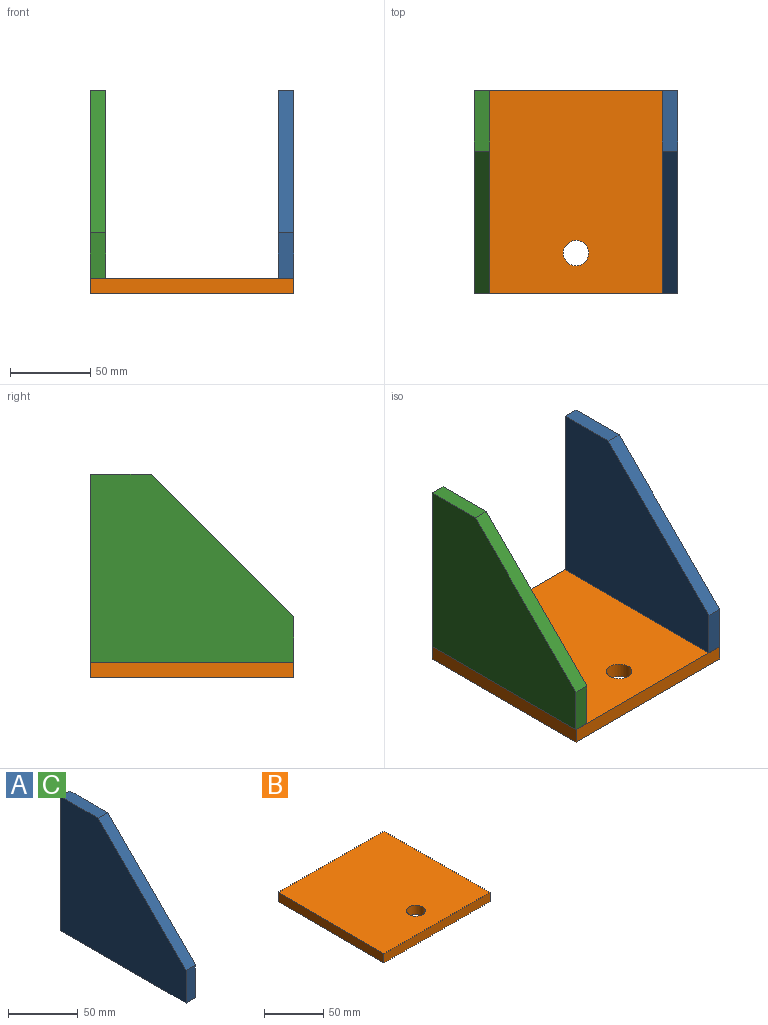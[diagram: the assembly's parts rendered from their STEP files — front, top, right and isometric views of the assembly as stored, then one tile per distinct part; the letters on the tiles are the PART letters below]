
ASSEMBLY  parts=3 mates=1
PART A: 7 faces, bbox 9.5x127x117.5 mm
  f0: plane 88.9x88.9mm, normal (0,-0.71,0.71), area 1197.5mm2, adj f1,f2,f4,f5
  f1: plane 38.1x9.53mm, normal (0,0,1), area 362.9mm2, adj f0,f2,f3,f4
  f2: plane 127x117.48mm, normal (-1,0,0), area 10967.7mm2, adj f0,f1,f3,f5,f6
  f3: plane 117.48x9.53mm, normal (0,1,0), area 1118.9mm2, adj f1,f2,f4,f6
  f4: plane 127x117.48mm, normal (1,0,0), area 10967.7mm2, adj f0,f1,f3,f5,f6
  f5: plane 28.58x9.53mm, normal (0,-1,0), area 272.2mm2, adj f0,f2,f4,f6
  f6: plane 127x9.53mm, normal (0,0,-1), area 1209.7mm2, adj f2,f3,f4,f5
PART B: 7 faces, bbox 127x127x9.5 mm
  f0: plane 127x9.53mm, normal (0,-1,0), area 1209.7mm2, adj f1,f3,f4,f5
  f1: plane 127x9.53mm, normal (1,0,0), area 1209.7mm2, adj f0,f2,f4,f5
  f2: plane 127x9.53mm, normal (0,1,0), area 1209.7mm2, adj f1,f3,f4,f5
  f3: plane 127x9.53mm, normal (-1,0,0), area 1209.7mm2, adj f0,f2,f4,f5
  f4: plane 127x127mm, normal (0,0,-1), area 15931.1mm2, adj f0,f1,f2,f3,f6
  f5: plane 127x127mm, normal (0,0,1), area 15931.1mm2, adj f0,f1,f2,f3,f6
  f6: cylinder r=7.94mm len=15.88mm, axis (0,0,1), area 475mm2, adj f4,f5
PART C: same geometry as A
PLACE A t=(-26.06,-109.54,-482.25)mm
PLACE B t=(-26.06,-109.54,-482.25)mm
PLACE C t=(-143.54,-109.54,-482.25)mm
MATE fastened B.f3 <-> C.f2  axis (-1,0,0) through (-89.56,-744.54,-320.32)mm
